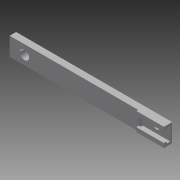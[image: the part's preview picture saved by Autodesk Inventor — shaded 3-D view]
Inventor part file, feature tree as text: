
AUTODESK INVENTOR PART (.ipt)
format: ipt  version: 2013 (Build 170138000, 138)  size: 163,840 bytes
history: native  units: in
note: dims shown in document units (in); Inventor stores cm internally (conversion verified against a paired STEP export)
features: extrude x9, sketch x8
ambient origin geometry x8: Origin, YZ Plane, XZ Plane, XY Plane, X Axis, Y Axis, Z Axis, Center Point
bodies: Solid1 (feature_tree)
feature tree (17):
  extrude  "Extrusion1"  Depth=1.0in
  extrude  "Extrusion2"  Depth=1.5in
  extrude  "Extrusion3"  Depth=0.365in
  extrude  "Extrusion4"  Depth=0.35in TaperAngle=0.0deg
  extrude  "Extrusion5"  Depth=0.1in TaperAngle=0.0deg
  sketch  "Sketch6"  dims[d14=0.2in d15=0.1in d16=0.0in]
  extrude  "Extrusion6"  Depth=0.1in TaperAngle=0.0deg
  extrude  "Extrusion7"  Depth=0.1in TaperAngle=0.0deg
  extrude  "Extrusion8"  Depth=1.5in
  extrude  "Extrusion9"  Depth=0.35in
  sketch  "Sketch1"  dims[d0=8.5in d1=1.0in]
  sketch  "Sketch2"  dims[d2=0.35in d3=0.0in d4=1.5in]
  sketch  "Sketch3"  dims[d5=0.365in d6=0.365in]
  sketch  "Sketch4"  dims[d7=0.35in d8=0.0in d9=0.35in d10=0.0in]
  sketch  "Sketch5"  dims[d11=0.2in d12=0.1in d13=0.0in]
  sketch  "Sketch7"  dims[d19=0.15in d20=0.1in d21=0.0in]
  sketch  "Sketch8"  dims[d22=0.1in d23=0.0in d24=1.5in d25=0.35in d26=0.1in d27=0.0in d28=0.5in d29=1.0in d30=0.0in]
